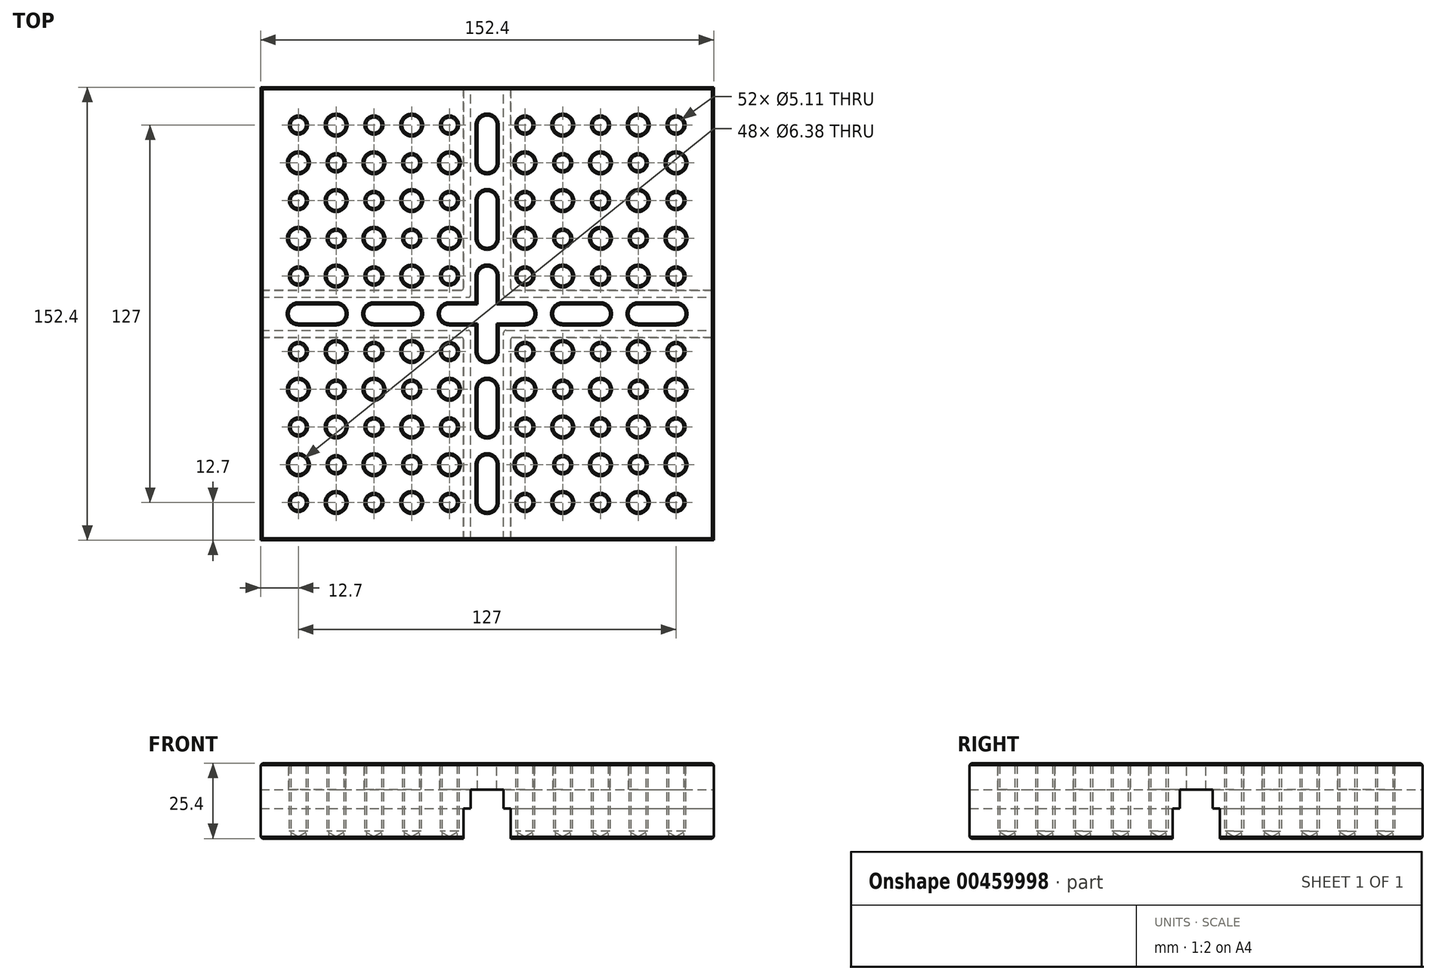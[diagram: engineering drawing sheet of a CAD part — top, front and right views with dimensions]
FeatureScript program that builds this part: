
annotation { "Feature Type Name" : "Feature", "Feature Type Description" : "" }
export const myFeature = defineFeature(function(context is Context, id is Id, definition is map)
    precondition{}
    {
        {
            var Q0;
            Q0=qCreatedBy(makeId("Top.planeOp"),FACE);
            var sketch = newSketch(context, id + "F0", { "sketchPlane" : qUnion([Q0])});
            skLineSegment(sketch, "E0.bottom", {"start": v(-76.2, -76.2) * mm, "end": v(76.2, -76.2) * mm});
            skLineSegment(sketch, "E0.top", {"start": v(-76.2, 76.2) * mm, "end": v(76.2, 76.2) * mm});
            skLineSegment(sketch, "E0.left", {"start": v(-76.2, -76.2) * mm, "end": v(-76.2, 76.2) * mm});
            skLineSegment(sketch, "E0.right", {"start": v(76.2, -76.2) * mm, "end": v(76.2, 76.2) * mm});
            skPoint(sketch, "E0.middle", {"position": v(0, 0) * mm});
            skSolve(sketch);
        }
        {
            var Q0;
            Q0 = qSketchRegion(id + "F0", true);
            extrude(context, id + "F1", {"entities" : qUnion([Q0]), "oppositeDirection" : true, "depth" : 25.4 * mm});
        }
        {
            var Q0;
            Q0=makeQuery(id+"F1.opExtrude","CAP_FACE",FACE,{"disambiguationData":[OSD([sQuery(id+"F0.wireOp",EDGE,"E0.bottom"),sQuery(id+"F0.wireOp",EDGE,"E0.top"),sQuery(id+"F0.wireOp",EDGE,"E0.left"),sQuery(id+"F0.wireOp",EDGE,"E0.right")])],"isStart":true});
            var sketch = newSketch(context, id + "F2", { "sketchPlane" : qUnion([Q0])});
            skPoint(sketch, "E1", {"position": v(-63.5, -63.5) * mm});
            skPoint(sketch, "E2.0.1.0", {"position": v(-63.5, -50.8) * mm});
            skPoint(sketch, "E2.0.2.0", {"position": v(-63.5, -38.1) * mm});
            skPoint(sketch, "E2.0.3.0", {"position": v(-63.5, -25.4) * mm});
            skPoint(sketch, "E2.0.4.0", {"position": v(-63.5, -12.7) * mm});
            skPoint(sketch, "E2.0.5.0", {"position": v(-63.5, 0) * mm});
            skPoint(sketch, "E2.0.6.0", {"position": v(-63.5, 12.7) * mm});
            skPoint(sketch, "E2.0.7.0", {"position": v(-63.5, 25.4) * mm});
            skPoint(sketch, "E2.0.8.0", {"position": v(-63.5, 38.1) * mm});
            skPoint(sketch, "E2.0.9.0", {"position": v(-63.5, 50.8) * mm});
            skPoint(sketch, "E2.0.10.0", {"position": v(-63.5, 63.5) * mm});
            skPoint(sketch, "E2.1.0.0", {"position": v(-50.8, -63.5) * mm});
            skPoint(sketch, "E2.1.1.0", {"position": v(-50.8, -50.8) * mm});
            skPoint(sketch, "E2.1.2.0", {"position": v(-50.8, -38.1) * mm});
            skPoint(sketch, "E2.1.3.0", {"position": v(-50.8, -25.4) * mm});
            skPoint(sketch, "E2.1.4.0", {"position": v(-50.8, -12.7) * mm});
            skPoint(sketch, "E2.1.5.0", {"position": v(-50.8, 0) * mm});
            skPoint(sketch, "E2.1.6.0", {"position": v(-50.8, 12.7) * mm});
            skPoint(sketch, "E2.1.7.0", {"position": v(-50.8, 25.4) * mm});
            skPoint(sketch, "E2.1.8.0", {"position": v(-50.8, 38.1) * mm});
            skPoint(sketch, "E2.1.9.0", {"position": v(-50.8, 50.8) * mm});
            skPoint(sketch, "E2.1.10.0", {"position": v(-50.8, 63.5) * mm});
            skPoint(sketch, "E2.2.0.0", {"position": v(-38.1, -63.5) * mm});
            skPoint(sketch, "E2.2.1.0", {"position": v(-38.1, -50.8) * mm});
            skPoint(sketch, "E2.2.2.0", {"position": v(-38.1, -38.1) * mm});
            skPoint(sketch, "E2.2.3.0", {"position": v(-38.1, -25.4) * mm});
            skPoint(sketch, "E2.2.4.0", {"position": v(-38.1, -12.7) * mm});
            skPoint(sketch, "E2.2.5.0", {"position": v(-38.1, 0) * mm});
            skPoint(sketch, "E2.2.6.0", {"position": v(-38.1, 12.7) * mm});
            skPoint(sketch, "E2.2.7.0", {"position": v(-38.1, 25.4) * mm});
            skPoint(sketch, "E2.2.8.0", {"position": v(-38.1, 38.1) * mm});
            skPoint(sketch, "E2.2.9.0", {"position": v(-38.1, 50.8) * mm});
            skPoint(sketch, "E2.2.10.0", {"position": v(-38.1, 63.5) * mm});
            skPoint(sketch, "E2.3.0.0", {"position": v(-25.4, -63.5) * mm});
            skPoint(sketch, "E2.3.1.0", {"position": v(-25.4, -50.8) * mm});
            skPoint(sketch, "E2.3.2.0", {"position": v(-25.4, -38.1) * mm});
            skPoint(sketch, "E2.3.3.0", {"position": v(-25.4, -25.4) * mm});
            skPoint(sketch, "E2.3.4.0", {"position": v(-25.4, -12.7) * mm});
            skPoint(sketch, "E2.3.5.0", {"position": v(-25.4, 0) * mm});
            skPoint(sketch, "E2.3.6.0", {"position": v(-25.4, 12.7) * mm});
            skPoint(sketch, "E2.3.7.0", {"position": v(-25.4, 25.4) * mm});
            skPoint(sketch, "E2.3.8.0", {"position": v(-25.4, 38.1) * mm});
            skPoint(sketch, "E2.3.9.0", {"position": v(-25.4, 50.8) * mm});
            skPoint(sketch, "E2.3.10.0", {"position": v(-25.4, 63.5) * mm});
            skPoint(sketch, "E2.4.0.0", {"position": v(-12.7, -63.5) * mm});
            skPoint(sketch, "E2.4.1.0", {"position": v(-12.7, -50.8) * mm});
            skPoint(sketch, "E2.4.2.0", {"position": v(-12.7, -38.1) * mm});
            skPoint(sketch, "E2.4.3.0", {"position": v(-12.7, -25.4) * mm});
            skPoint(sketch, "E2.4.4.0", {"position": v(-12.7, -12.7) * mm});
            skPoint(sketch, "E2.4.5.0", {"position": v(-12.7, 0) * mm});
            skPoint(sketch, "E2.4.6.0", {"position": v(-12.7, 12.7) * mm});
            skPoint(sketch, "E2.4.7.0", {"position": v(-12.7, 25.4) * mm});
            skPoint(sketch, "E2.4.8.0", {"position": v(-12.7, 38.1) * mm});
            skPoint(sketch, "E2.4.9.0", {"position": v(-12.7, 50.8) * mm});
            skPoint(sketch, "E2.4.10.0", {"position": v(-12.7, 63.5) * mm});
            skPoint(sketch, "E2.5.0.0", {"position": v(0, -63.5) * mm});
            skPoint(sketch, "E2.5.1.0", {"position": v(0, -50.8) * mm});
            skPoint(sketch, "E2.5.2.0", {"position": v(0, -38.1) * mm});
            skPoint(sketch, "E2.5.3.0", {"position": v(0, -25.4) * mm});
            skPoint(sketch, "E2.5.4.0", {"position": v(0, -12.7) * mm});
            skPoint(sketch, "E2.5.5.0", {"position": v(0, 0) * mm});
            skPoint(sketch, "E2.5.6.0", {"position": v(0, 12.7) * mm});
            skPoint(sketch, "E2.5.7.0", {"position": v(0, 25.4) * mm});
            skPoint(sketch, "E2.5.8.0", {"position": v(0, 38.1) * mm});
            skPoint(sketch, "E2.5.9.0", {"position": v(0, 50.8) * mm});
            skPoint(sketch, "E2.5.10.0", {"position": v(0, 63.5) * mm});
            skPoint(sketch, "E2.6.0.0", {"position": v(12.7, -63.5) * mm});
            skPoint(sketch, "E2.6.1.0", {"position": v(12.7, -50.8) * mm});
            skPoint(sketch, "E2.6.2.0", {"position": v(12.7, -38.1) * mm});
            skPoint(sketch, "E2.6.3.0", {"position": v(12.7, -25.4) * mm});
            skPoint(sketch, "E2.6.4.0", {"position": v(12.7, -12.7) * mm});
            skPoint(sketch, "E2.6.5.0", {"position": v(12.7, 0) * mm});
            skPoint(sketch, "E2.6.6.0", {"position": v(12.7, 12.7) * mm});
            skPoint(sketch, "E2.6.7.0", {"position": v(12.7, 25.4) * mm});
            skPoint(sketch, "E2.6.8.0", {"position": v(12.7, 38.1) * mm});
            skPoint(sketch, "E2.6.9.0", {"position": v(12.7, 50.8) * mm});
            skPoint(sketch, "E2.6.10.0", {"position": v(12.7, 63.5) * mm});
            skPoint(sketch, "E2.7.0.0", {"position": v(25.4, -63.5) * mm});
            skPoint(sketch, "E2.7.1.0", {"position": v(25.4, -50.8) * mm});
            skPoint(sketch, "E2.7.2.0", {"position": v(25.4, -38.1) * mm});
            skPoint(sketch, "E2.7.3.0", {"position": v(25.4, -25.4) * mm});
            skPoint(sketch, "E2.7.4.0", {"position": v(25.4, -12.7) * mm});
            skPoint(sketch, "E2.7.5.0", {"position": v(25.4, 0) * mm});
            skPoint(sketch, "E2.7.6.0", {"position": v(25.4, 12.7) * mm});
            skPoint(sketch, "E2.7.7.0", {"position": v(25.4, 25.4) * mm});
            skPoint(sketch, "E2.7.8.0", {"position": v(25.4, 38.1) * mm});
            skPoint(sketch, "E2.7.9.0", {"position": v(25.4, 50.8) * mm});
            skPoint(sketch, "E2.7.10.0", {"position": v(25.4, 63.5) * mm});
            skPoint(sketch, "E2.8.0.0", {"position": v(38.1, -63.5) * mm});
            skPoint(sketch, "E2.8.1.0", {"position": v(38.1, -50.8) * mm});
            skPoint(sketch, "E2.8.2.0", {"position": v(38.1, -38.1) * mm});
            skPoint(sketch, "E2.8.3.0", {"position": v(38.1, -25.4) * mm});
            skPoint(sketch, "E2.8.4.0", {"position": v(38.1, -12.7) * mm});
            skPoint(sketch, "E2.8.5.0", {"position": v(38.1, 0) * mm});
            skPoint(sketch, "E2.8.6.0", {"position": v(38.1, 12.7) * mm});
            skPoint(sketch, "E2.8.7.0", {"position": v(38.1, 25.4) * mm});
            skPoint(sketch, "E2.8.8.0", {"position": v(38.1, 38.1) * mm});
            skPoint(sketch, "E2.8.9.0", {"position": v(38.1, 50.8) * mm});
            skPoint(sketch, "E2.8.10.0", {"position": v(38.1, 63.5) * mm});
            skPoint(sketch, "E2.9.0.0", {"position": v(50.8, -63.5) * mm});
            skPoint(sketch, "E2.9.1.0", {"position": v(50.8, -50.8) * mm});
            skPoint(sketch, "E2.9.2.0", {"position": v(50.8, -38.1) * mm});
            skPoint(sketch, "E2.9.3.0", {"position": v(50.8, -25.4) * mm});
            skPoint(sketch, "E2.9.4.0", {"position": v(50.8, -12.7) * mm});
            skPoint(sketch, "E2.9.5.0", {"position": v(50.8, 0) * mm});
            skPoint(sketch, "E2.9.6.0", {"position": v(50.8, 12.7) * mm});
            skPoint(sketch, "E2.9.7.0", {"position": v(50.8, 25.4) * mm});
            skPoint(sketch, "E2.9.8.0", {"position": v(50.8, 38.1) * mm});
            skPoint(sketch, "E2.9.9.0", {"position": v(50.8, 50.8) * mm});
            skPoint(sketch, "E2.9.10.0", {"position": v(50.8, 63.5) * mm});
            skPoint(sketch, "E2.10.0.0", {"position": v(63.5, -63.5) * mm});
            skPoint(sketch, "E2.10.1.0", {"position": v(63.5, -50.8) * mm});
            skPoint(sketch, "E2.10.2.0", {"position": v(63.5, -38.1) * mm});
            skPoint(sketch, "E2.10.3.0", {"position": v(63.5, -25.4) * mm});
            skPoint(sketch, "E2.10.4.0", {"position": v(63.5, -12.7) * mm});
            skPoint(sketch, "E2.10.5.0", {"position": v(63.5, 0) * mm});
            skPoint(sketch, "E2.10.6.0", {"position": v(63.5, 12.7) * mm});
            skPoint(sketch, "E2.10.7.0", {"position": v(63.5, 25.4) * mm});
            skPoint(sketch, "E2.10.8.0", {"position": v(63.5, 38.1) * mm});
            skPoint(sketch, "E2.10.9.0", {"position": v(63.5, 50.8) * mm});
            skPoint(sketch, "E2.10.10.0", {"position": v(63.5, 63.5) * mm});
            skLineSegment(sketch, "E2.direction1", {"start": v(-63.5, -63.5) * mm, "end": v(-50.8, -63.5) * mm, "construction": true});
            skLineSegment(sketch, "E2.direction2", {"start": v(-63.5, -63.5) * mm, "end": v(-63.5, -50.8) * mm, "construction": true});
            skSolve(sketch);
        }
        {
            var Q0;
            Q0=sQuery(id+"F2.wireOp",VERTEX,"E2.0.10.0");
            var Q1;
            Q1=sQuery(id+"F2.wireOp",VERTEX,"E2.2.10.0");
            var Q2;
            Q2=sQuery(id+"F2.wireOp",VERTEX,"E2.4.10.0");
            var Q3;
            Q3=sQuery(id+"F2.wireOp",VERTEX,"E2.6.10.0");
            var Q4;
            Q4=sQuery(id+"F2.wireOp",VERTEX,"E2.8.10.0");
            var Q5;
            Q5=sQuery(id+"F2.wireOp",VERTEX,"E2.10.10.0");
            var Q6;
            Q6=sQuery(id+"F2.wireOp",VERTEX,"E2.1.9.0");
            var Q7;
            Q7=sQuery(id+"F2.wireOp",VERTEX,"E2.3.9.0");
            var Q8;
            Q8=sQuery(id+"F2.wireOp",VERTEX,"E2.7.9.0");
            var Q9;
            Q9=sQuery(id+"F2.wireOp",VERTEX,"E2.9.9.0");
            var Q10;
            Q10=sQuery(id+"F2.wireOp",VERTEX,"E2.0.8.0");
            var Q11;
            Q11=sQuery(id+"F2.wireOp",VERTEX,"E2.2.8.0");
            var Q12;
            Q12=sQuery(id+"F2.wireOp",VERTEX,"E2.4.8.0");
            var Q13;
            Q13=sQuery(id+"F2.wireOp",VERTEX,"E2.6.8.0");
            var Q14;
            Q14=sQuery(id+"F2.wireOp",VERTEX,"E2.10.8.0");
            var Q15;
            Q15=sQuery(id+"F2.wireOp",VERTEX,"E2.8.8.0");
            var Q16;
            Q16=sQuery(id+"F2.wireOp",VERTEX,"E2.1.7.0");
            var Q17;
            Q17=sQuery(id+"F2.wireOp",VERTEX,"E2.3.7.0");
            var Q18;
            Q18=sQuery(id+"F2.wireOp",VERTEX,"E2.3.7.0");
            var Q19;
            Q19=sQuery(id+"F2.wireOp",VERTEX,"E2.7.7.0");
            var Q20;
            Q20=sQuery(id+"F2.wireOp",VERTEX,"E2.9.7.0");
            var Q21;
            Q21=sQuery(id+"F2.wireOp",VERTEX,"E2.0.6.0");
            var Q22;
            Q22=sQuery(id+"F2.wireOp",VERTEX,"E2.2.6.0");
            var Q23;
            Q23=sQuery(id+"F2.wireOp",VERTEX,"E2.4.6.0");
            var Q24;
            Q24=sQuery(id+"F2.wireOp",VERTEX,"E2.6.6.0");
            var Q25;
            Q25=sQuery(id+"F2.wireOp",VERTEX,"E2.8.6.0");
            var Q26;
            Q26=sQuery(id+"F2.wireOp",VERTEX,"E2.10.6.0");
            var Q27;
            Q27=makeQuery(id+"F1.opExtrude","SWEPT_BODY",BODY,{"disambiguationData":[OSD([sQuery(id+"F0.wireOp",EDGE,"E0.bottom"),sQuery(id+"F0.wireOp",EDGE,"E0.top"),sQuery(id+"F0.wireOp",EDGE,"E0.left"),sQuery(id+"F0.wireOp",EDGE,"E0.right")])]});
            hole(context, id + "F3", {"style" : HoleStyle.SIMPLE, "endStyle" : HoleEndStyle.THROUGH, "standardTappedOrClearance" : lookupTablePath({ "standard" : "ANSI", "engagement" : "75%", "pitch" : "20 tpi", "size" : "1/4", "type" : "Tapped" }), "standardBlindInLast" : lookupTablePath({ "standard" : "ANSI", "engagement" : "75%", "pitch" : "20 tpi", "size" : "1/4", "type" : "Tapped" }), "holeDiameter" : 5.1 * mm, "showTappedDepth" : true, "isTappedThrough" : true, "tappedDepth" : 19.05 * mm, "tapClearance" : 3, "locations" : qUnion([Q0, Q1, Q2, Q3, Q4, Q5, Q6, Q7, Q8, Q9, Q10, Q11, Q12, Q13, Q14, Q15, Q16, Q17, Q18, Q19, Q20, Q21, Q22, Q23, Q24, Q25, Q26]), "scope" : qUnion([Q27]), "majorDiameter" : 6.35 * mm, "startStyle" : HoleStartStyle.PART});
        }
        {
            var Q0;
            Q0=sQuery(id+"F2.wireOp",VERTEX,"E2.0.4.0");
            var Q1;
            Q1=sQuery(id+"F2.wireOp",VERTEX,"E2.2.4.0");
            var Q2;
            Q2=sQuery(id+"F2.wireOp",VERTEX,"E2.4.4.0");
            var Q3;
            Q3=sQuery(id+"F2.wireOp",VERTEX,"E2.6.4.0");
            var Q4;
            Q4=sQuery(id+"F2.wireOp",VERTEX,"E2.8.4.0");
            var Q5;
            Q5=sQuery(id+"F2.wireOp",VERTEX,"E2.10.4.0");
            var Q6;
            Q6=sQuery(id+"F2.wireOp",VERTEX,"E2.1.3.0");
            var Q7;
            Q7=sQuery(id+"F2.wireOp",VERTEX,"E2.3.3.0");
            var Q8;
            Q8=sQuery(id+"F2.wireOp",VERTEX,"E2.7.3.0");
            var Q9;
            Q9=sQuery(id+"F2.wireOp",VERTEX,"E2.9.3.0");
            var Q10;
            Q10=sQuery(id+"F2.wireOp",VERTEX,"E2.10.2.0");
            var Q11;
            Q11=sQuery(id+"F2.wireOp",VERTEX,"E2.8.2.0");
            var Q12;
            Q12=sQuery(id+"F2.wireOp",VERTEX,"E2.6.2.0");
            var Q13;
            Q13=sQuery(id+"F2.wireOp",VERTEX,"E2.4.2.0");
            var Q14;
            Q14=sQuery(id+"F2.wireOp",VERTEX,"E2.2.2.0");
            var Q15;
            Q15=sQuery(id+"F2.wireOp",VERTEX,"E2.0.2.0");
            var Q16;
            Q16=sQuery(id+"F2.wireOp",VERTEX,"E2.1.1.0");
            var Q17;
            Q17=sQuery(id+"F2.wireOp",VERTEX,"E2.3.1.0");
            var Q18;
            Q18=sQuery(id+"F2.wireOp",VERTEX,"E2.9.1.0");
            var Q19;
            Q19=sQuery(id+"F2.wireOp",VERTEX,"E2.7.1.0");
            var Q20;
            Q20=sQuery(id+"F2.wireOp",VERTEX,"E1");
            var Q21;
            Q21=sQuery(id+"F2.wireOp",VERTEX,"E2.2.0.0");
            var Q22;
            Q22=sQuery(id+"F2.wireOp",VERTEX,"E2.4.0.0");
            var Q23;
            Q23=sQuery(id+"F2.wireOp",VERTEX,"E2.6.0.0");
            var Q24;
            Q24=sQuery(id+"F2.wireOp",VERTEX,"E2.8.0.0");
            var Q25;
            Q25=sQuery(id+"F2.wireOp",VERTEX,"E2.10.0.0");
            var Q26;
            Q26=makeQuery(id+"F1.opExtrude","SWEPT_BODY",BODY,{"disambiguationData":[OSD([sQuery(id+"F0.wireOp",EDGE,"E0.bottom"),sQuery(id+"F0.wireOp",EDGE,"E0.top"),sQuery(id+"F0.wireOp",EDGE,"E0.left"),sQuery(id+"F0.wireOp",EDGE,"E0.right")])]});
            hole(context, id + "F4", {"style" : HoleStyle.SIMPLE, "endStyle" : HoleEndStyle.THROUGH, "standardTappedOrClearance" : lookupTablePath({ "standard" : "ANSI", "engagement" : "75%", "pitch" : "20 tpi", "size" : "1/4", "type" : "Tapped" }), "standardBlindInLast" : lookupTablePath({ "standard" : "ANSI", "engagement" : "75%", "pitch" : "20 tpi", "size" : "1/4", "type" : "Tapped" }), "holeDiameter" : 5.1 * mm, "showTappedDepth" : true, "isTappedThrough" : true, "tappedDepth" : 19.05 * mm, "tapClearance" : 3, "locations" : qUnion([Q0, Q1, Q2, Q3, Q4, Q5, Q6, Q7, Q8, Q9, Q10, Q11, Q12, Q13, Q14, Q15, Q16, Q17, Q18, Q19, Q20, Q21, Q22, Q23, Q24, Q25]), "scope" : qUnion([Q26]), "majorDiameter" : 6.35 * mm, "startStyle" : HoleStartStyle.PART});
        }
        {
            var Q0;
            Q0=sQuery(id+"F2.wireOp",VERTEX,"E2.1.10.0");
            var Q1;
            Q1=sQuery(id+"F2.wireOp",VERTEX,"E2.3.10.0");
            var Q2;
            Q2=sQuery(id+"F2.wireOp",VERTEX,"E2.7.10.0");
            var Q3;
            Q3=sQuery(id+"F2.wireOp",VERTEX,"E2.9.10.0");
            var Q4;
            Q4=sQuery(id+"F2.wireOp",VERTEX,"E2.9.8.0");
            var Q5;
            Q5=sQuery(id+"F2.wireOp",VERTEX,"E2.8.9.0");
            var Q6;
            Q6=sQuery(id+"F2.wireOp",VERTEX,"E2.6.9.0");
            var Q7;
            Q7=sQuery(id+"F2.wireOp",VERTEX,"E2.4.9.0");
            var Q8;
            Q8=sQuery(id+"F2.wireOp",VERTEX,"E2.0.9.0");
            var Q9;
            Q9=sQuery(id+"F2.wireOp",VERTEX,"E2.1.8.0");
            var Q10;
            Q10=sQuery(id+"F2.wireOp",VERTEX,"E2.2.9.0");
            var Q11;
            Q11=sQuery(id+"F2.wireOp",VERTEX,"E2.3.8.0");
            var Q12;
            Q12=sQuery(id+"F2.wireOp",VERTEX,"E2.7.8.0");
            var Q13;
            Q13=sQuery(id+"F2.wireOp",VERTEX,"E2.10.9.0");
            var Q14;
            Q14=sQuery(id+"F2.wireOp",VERTEX,"E2.10.7.0");
            var Q15;
            Q15=sQuery(id+"F2.wireOp",VERTEX,"E2.8.7.0");
            var Q16;
            Q16=sQuery(id+"F2.wireOp",VERTEX,"E2.10.7.0");
            var Q17;
            Q17=sQuery(id+"F2.wireOp",VERTEX,"E2.6.7.0");
            var Q18;
            Q18=sQuery(id+"F2.wireOp",VERTEX,"E2.4.7.0");
            var Q19;
            Q19=sQuery(id+"F2.wireOp",VERTEX,"E2.0.7.0");
            var Q20;
            Q20=sQuery(id+"F2.wireOp",VERTEX,"E2.3.6.0");
            var Q21;
            Q21=sQuery(id+"F2.wireOp",VERTEX,"E2.1.6.0");
            var Q22;
            Q22=sQuery(id+"F2.wireOp",VERTEX,"E2.2.7.0");
            var Q23;
            Q23=sQuery(id+"F2.wireOp",VERTEX,"E2.7.6.0");
            var Q24;
            Q24=sQuery(id+"F2.wireOp",VERTEX,"E2.9.6.0");
            var Q25;
            Q25=sQuery(id+"F2.wireOp",VERTEX,"E2.1.4.0");
            var Q26;
            Q26=sQuery(id+"F2.wireOp",VERTEX,"E2.3.4.0");
            var Q27;
            Q27=sQuery(id+"F2.wireOp",VERTEX,"E2.4.3.0");
            var Q28;
            Q28=sQuery(id+"F2.wireOp",VERTEX,"E2.2.3.0");
            var Q29;
            Q29=sQuery(id+"F2.wireOp",VERTEX,"E2.0.3.0");
            var Q30;
            Q30=sQuery(id+"F2.wireOp",VERTEX,"E2.1.2.0");
            var Q31;
            Q31=sQuery(id+"F2.wireOp",VERTEX,"E2.3.2.0");
            var Q32;
            Q32=sQuery(id+"F2.wireOp",VERTEX,"E2.0.1.0");
            var Q33;
            Q33=sQuery(id+"F2.wireOp",VERTEX,"E2.2.1.0");
            var Q34;
            Q34=sQuery(id+"F2.wireOp",VERTEX,"E2.4.1.0");
            var Q35;
            Q35=sQuery(id+"F2.wireOp",VERTEX,"E2.3.0.0");
            var Q36;
            Q36=sQuery(id+"F2.wireOp",VERTEX,"E2.1.0.0");
            var Q37;
            Q37=sQuery(id+"F2.wireOp",VERTEX,"E2.3.0.0");
            var Q38;
            Q38=sQuery(id+"F2.wireOp",VERTEX,"E2.7.0.0");
            var Q39;
            Q39=sQuery(id+"F2.wireOp",VERTEX,"E2.6.1.0");
            var Q40;
            Q40=sQuery(id+"F2.wireOp",VERTEX,"E2.6.3.0");
            var Q41;
            Q41=sQuery(id+"F2.wireOp",VERTEX,"E2.7.4.0");
            var Q42;
            Q42=sQuery(id+"F2.wireOp",VERTEX,"E2.7.2.0");
            var Q43;
            Q43=sQuery(id+"F2.wireOp",VERTEX,"E2.8.3.0");
            var Q44;
            Q44=sQuery(id+"F2.wireOp",VERTEX,"E2.9.4.0");
            var Q45;
            Q45=sQuery(id+"F2.wireOp",VERTEX,"E2.10.3.0");
            var Q46;
            Q46=sQuery(id+"F2.wireOp",VERTEX,"E2.8.1.0");
            var Q47;
            Q47=sQuery(id+"F2.wireOp",VERTEX,"E2.9.2.0");
            var Q48;
            Q48=sQuery(id+"F2.wireOp",VERTEX,"E2.10.1.0");
            var Q49;
            Q49=sQuery(id+"F2.wireOp",VERTEX,"E2.9.0.0");
            var Q50;
            Q50=makeQuery(id+"F1.opExtrude","SWEPT_BODY",BODY,{"disambiguationData":[OSD([sQuery(id+"F0.wireOp",EDGE,"E0.bottom"),sQuery(id+"F0.wireOp",EDGE,"E0.top"),sQuery(id+"F0.wireOp",EDGE,"E0.left"),sQuery(id+"F0.wireOp",EDGE,"E0.right")])]});
            hole(context, id + "F5", {"style" : HoleStyle.SIMPLE, "endStyle" : HoleEndStyle.BLIND, "holeDiameter" : 6.38 * mm, "holeDepth" : 22.86 * mm, "isTappedThrough" : true, "tappedDepth" : 19.05 * mm, "tapClearance" : 3, "locations" : qUnion([Q0, Q1, Q2, Q3, Q4, Q5, Q6, Q7, Q8, Q9, Q10, Q11, Q12, Q13, Q14, Q15, Q16, Q17, Q18, Q19, Q20, Q21, Q22, Q23, Q24, Q25, Q26, Q27, Q28, Q29, Q30, Q31, Q32, Q33, Q34, Q35, Q36, Q37, Q38, Q39, Q40, Q41, Q42, Q43, Q44, Q45, Q46, Q47, Q48, Q49]), "scope" : qUnion([Q50]), "startStyle" : HoleStartStyle.PART});
        }
        {
            var Q0;
            Q0=makeQuery(id+"F2.imprint","IMPRINT",FACE,{"disambiguationData":[TD([[makeQuery(id+"F2.imprint","IMPRINT",EDGE,{"derivedFrom":makeQuery(id+"F1.opExtrude","CAP_EDGE",EDGE,{"disambiguationData":[OSD([sQuery(id+"F0.wireOp",EDGE,"E0.bottom")])],"isStart":true})}),1.0]])]});
            var sketch = newSketch(context, id + "F6", { "sketchPlane" : qUnion([Q0])});
            skLineSegment(sketch, "E3", {"start": v(0, 63.5) * mm, "end": v(0, 50.8) * mm});
            skLineSegment(sketch, "E4", {"start": v(0, 38.1) * mm, "end": v(0, 25.4) * mm});
            skLineSegment(sketch, "E5", {"start": v(0, 12.7) * mm, "end": v(0, -12.7) * mm});
            skLineSegment(sketch, "E6", {"start": v(12.7, 0) * mm, "end": v(-12.7, 0) * mm});
            skLineSegment(sketch, "E7", {"start": v(-25.4, 0) * mm, "end": v(-38.1, 0) * mm});
            skLineSegment(sketch, "E8", {"start": v(-50.8, 0) * mm, "end": v(-63.5, 0) * mm});
            skLineSegment(sketch, "E9", {"start": v(25.4, 0) * mm, "end": v(38.1, 0) * mm});
            skLineSegment(sketch, "E10", {"start": v(50.8, 0) * mm, "end": v(63.5, 0) * mm});
            skLineSegment(sketch, "E11.MirrorCS", {"start": v(0, -38.1) * mm, "end": v(0, -25.4) * mm});
            skLineSegment(sketch, "E12.MirrorCS", {"start": v(0, -63.5) * mm, "end": v(0, -50.8) * mm});
            skArc(sketch, "E13.0.startCap", {"start": v(-3.24, 63.5) * mm, "mid": v(0, 66.74) * mm, "end": v(3.24, 63.5) * mm});
            skArc(sketch, "E13.0.endCap", {"start": v(3.24, 50.8) * mm, "mid": v(0, 47.56) * mm, "end": v(-3.24, 50.8) * mm});
            skLineSegment(sketch, "E13.0.left", {"start": v(3.24, 63.5) * mm, "end": v(3.24, 50.8) * mm});
            skLineSegment(sketch, "E13.0.right", {"start": v(-3.24, 63.5) * mm, "end": v(-3.24, 50.8) * mm});
            skArc(sketch, "E14.0.startCap", {"start": v(-3.24, 38.1) * mm, "mid": v(0, 41.34) * mm, "end": v(3.24, 38.1) * mm});
            skArc(sketch, "E14.0.endCap", {"start": v(3.24, 25.4) * mm, "mid": v(0, 22.16) * mm, "end": v(-3.24, 25.4) * mm});
            skLineSegment(sketch, "E14.0.left", {"start": v(3.24, 38.1) * mm, "end": v(3.24, 25.4) * mm});
            skLineSegment(sketch, "E14.0.right", {"start": v(-3.24, 38.1) * mm, "end": v(-3.24, 25.4) * mm});
            skArc(sketch, "E14.1.startCap", {"start": v(-3.24, 12.7) * mm, "mid": v(0, 15.94) * mm, "end": v(3.24, 12.7) * mm});
            skArc(sketch, "E14.1.endCap", {"start": v(3.24, -12.7) * mm, "mid": v(0, -15.94) * mm, "end": v(-3.24, -12.7) * mm});
            skLineSegment(sketch, "E14.1.left", {"start": v(3.24, 12.7) * mm, "end": v(3.24, -12.7) * mm});
            skLineSegment(sketch, "E14.1.right", {"start": v(-3.24, 12.7) * mm, "end": v(-3.24, -12.7) * mm});
            skArc(sketch, "E14.2.startCap", {"start": v(12.7, 3.24) * mm, "mid": v(15.94, 0) * mm, "end": v(12.7, -3.24) * mm});
            skArc(sketch, "E14.2.endCap", {"start": v(-12.7, -3.24) * mm, "mid": v(-15.94, 0) * mm, "end": v(-12.7, 3.24) * mm});
            skLineSegment(sketch, "E14.2.left", {"start": v(12.7, -3.24) * mm, "end": v(-12.7, -3.24) * mm});
            skLineSegment(sketch, "E14.2.right", {"start": v(12.7, 3.24) * mm, "end": v(-12.7, 3.24) * mm});
            skArc(sketch, "E14.3.startCap", {"start": v(-25.4, 3.24) * mm, "mid": v(-22.16, 0) * mm, "end": v(-25.4, -3.24) * mm});
            skArc(sketch, "E14.3.endCap", {"start": v(-38.1, -3.24) * mm, "mid": v(-41.34, 0) * mm, "end": v(-38.1, 3.24) * mm});
            skLineSegment(sketch, "E14.3.left", {"start": v(-25.4, -3.24) * mm, "end": v(-38.1, -3.24) * mm});
            skLineSegment(sketch, "E14.3.right", {"start": v(-25.4, 3.24) * mm, "end": v(-38.1, 3.24) * mm});
            skArc(sketch, "E14.4.startCap", {"start": v(-50.8, 3.24) * mm, "mid": v(-47.56, 0) * mm, "end": v(-50.8, -3.24) * mm});
            skArc(sketch, "E14.4.endCap", {"start": v(-63.5, -3.24) * mm, "mid": v(-66.74, 0) * mm, "end": v(-63.5, 3.24) * mm});
            skLineSegment(sketch, "E14.4.left", {"start": v(-50.8, -3.24) * mm, "end": v(-63.5, -3.24) * mm});
            skLineSegment(sketch, "E14.4.right", {"start": v(-50.8, 3.24) * mm, "end": v(-63.5, 3.24) * mm});
            skArc(sketch, "E14.5.startCap", {"start": v(25.4, -3.24) * mm, "mid": v(22.16, 0) * mm, "end": v(25.4, 3.24) * mm});
            skArc(sketch, "E14.5.endCap", {"start": v(38.1, 3.24) * mm, "mid": v(41.34, 0) * mm, "end": v(38.1, -3.24) * mm});
            skLineSegment(sketch, "E14.5.left", {"start": v(25.4, 3.24) * mm, "end": v(38.1, 3.24) * mm});
            skLineSegment(sketch, "E14.5.right", {"start": v(25.4, -3.24) * mm, "end": v(38.1, -3.24) * mm});
            skArc(sketch, "E14.6.startCap", {"start": v(50.8, -3.24) * mm, "mid": v(47.56, 0) * mm, "end": v(50.8, 3.24) * mm});
            skArc(sketch, "E14.6.endCap", {"start": v(63.5, 3.24) * mm, "mid": v(66.74, 0) * mm, "end": v(63.5, -3.24) * mm});
            skLineSegment(sketch, "E14.6.left", {"start": v(50.8, 3.24) * mm, "end": v(63.5, 3.24) * mm});
            skLineSegment(sketch, "E14.6.right", {"start": v(50.8, -3.24) * mm, "end": v(63.5, -3.24) * mm});
            skArc(sketch, "E14.7.startCap", {"start": v(3.24, -38.1) * mm, "mid": v(0, -41.34) * mm, "end": v(-3.24, -38.1) * mm});
            skArc(sketch, "E14.7.endCap", {"start": v(-3.24, -25.4) * mm, "mid": v(0, -22.16) * mm, "end": v(3.24, -25.4) * mm});
            skLineSegment(sketch, "E14.7.left", {"start": v(-3.24, -38.1) * mm, "end": v(-3.24, -25.4) * mm});
            skLineSegment(sketch, "E14.7.right", {"start": v(3.24, -38.1) * mm, "end": v(3.24, -25.4) * mm});
            skArc(sketch, "E14.8.startCap", {"start": v(3.24, -63.5) * mm, "mid": v(0, -66.74) * mm, "end": v(-3.24, -63.5) * mm});
            skArc(sketch, "E14.8.endCap", {"start": v(-3.24, -50.8) * mm, "mid": v(0, -47.56) * mm, "end": v(3.24, -50.8) * mm});
            skLineSegment(sketch, "E14.8.left", {"start": v(-3.24, -63.5) * mm, "end": v(-3.24, -50.8) * mm});
            skLineSegment(sketch, "E14.8.right", {"start": v(3.24, -63.5) * mm, "end": v(3.24, -50.8) * mm});
            skSolve(sketch);
        }
        {
            var Q0;
            Q0 = qSketchRegion(id + "F6", true);
            var Q1;
            Q1 = qConstructionFilter(qBodyType(qCreatedBy(id + "F6" ,EDGE), BodyType.WIRE), ConstructionObject.NO);
            extrude(context, id + "F7", {"entities" : qUnion([Q0]), "operationType" : NewBodyOperationType.REMOVE, "surfaceEntities" : qUnion([Q1]), "endBound" : BoundingType.THROUGH_ALL, "oppositeDirection" : true, "depth" : 25.4 * mm});
        }
        {
            var Q0;
            Q0=makeQuery(id+"F1.opExtrude","CAP_FACE",FACE,{"disambiguationData":[OSD([sQuery(id+"F0.wireOp",EDGE,"E0.bottom"),sQuery(id+"F0.wireOp",EDGE,"E0.top"),sQuery(id+"F0.wireOp",EDGE,"E0.left"),sQuery(id+"F0.wireOp",EDGE,"E0.right")])],"isStart":true});
            var Q1;
            Q1=makeQuery(id+"F1.opExtrude","CAP_FACE",FACE,{"disambiguationData":[OSD([sQuery(id+"F0.wireOp",EDGE,"E0.bottom"),sQuery(id+"F0.wireOp",EDGE,"E0.top"),sQuery(id+"F0.wireOp",EDGE,"E0.left"),sQuery(id+"F0.wireOp",EDGE,"E0.right")])],"isStart":false});
            chamfer(context, id + "F8", {"entities" : qUnion([Q0, Q1]), "width" : 0.64 * mm, "tangentPropagation" : true});
        }
        {
            var Q0;
            Q0=makeQuery(id+"F1.opExtrude","SWEPT_FACE",FACE,{"disambiguationData":[OSD([sQuery(id+"F0.wireOp",EDGE,"E0.right")])]});
            var sketch = newSketch(context, id + "F9", { "sketchPlane" : qUnion([Q0])});
            skLineSegment(sketch, "E15.bottom", {"start": v(-7.94, -34.3) * mm, "end": v(7.94, -34.3) * mm});
            skLineSegment(sketch, "E15.top", {"start": v(-7.94, -15.24) * mm, "end": v(-5.56, -15.24) * mm});
            skLineSegment(sketch, "E15.left", {"start": v(-7.94, -34.3) * mm, "end": v(-7.94, -15.24) * mm});
            skLineSegment(sketch, "E15.right", {"start": v(7.94, -34.3) * mm, "end": v(7.94, -15.24) * mm});
            skPoint(sketch, "E15.middle", {"position": v(0, -24.77) * mm});
            skLineSegment(sketch, "E16.top", {"start": v(-5.56, -8.89) * mm, "end": v(5.56, -8.89) * mm});
            skLineSegment(sketch, "E16.left", {"start": v(-5.56, -15.24) * mm, "end": v(-5.56, -8.89) * mm});
            skLineSegment(sketch, "E16.right", {"start": v(5.56, -15.24) * mm, "end": v(5.56, -8.89) * mm});
            skPoint(sketch, "E16.middle", {"position": v(0, -15.24) * mm});
            skLineSegment(sketch, "E17.trimOffspring", {"start": v(5.56, -15.24) * mm, "end": v(7.94, -15.24) * mm});
            skPoint(sketch, "E16.bottom.end.orphan", {"position": v(5.56, -21.59) * mm});
            skPoint(sketch, "E16.bottom.start.orphan", {"position": v(-5.56, -21.59) * mm});
            skSolve(sketch);
        }
        {
            var Q0;
            Q0 = qSketchRegion(id + "F9", true);
            extrude(context, id + "F10", {"entities" : qUnion([Q0]), "operationType" : NewBodyOperationType.REMOVE, "endBound" : BoundingType.THROUGH_ALL, "oppositeDirection" : true, "depth" : 25.4 * mm});
        }
        {
            var Q0;
            Q0=makeQuery(id+"F1.opExtrude","SWEPT_FACE",FACE,{"disambiguationData":[OSD([sQuery(id+"F0.wireOp",EDGE,"E0.top")])]});
            var sketch = newSketch(context, id + "F11", { "sketchPlane" : qUnion([Q0])});
            skLineSegment(sketch, "E18.bottom", {"start": v(-7.94, -34.3) * mm, "end": v(7.94, -34.3) * mm});
            skLineSegment(sketch, "E18.top", {"start": v(-7.94, -15.24) * mm, "end": v(-5.56, -15.24) * mm});
            skLineSegment(sketch, "E18.left", {"start": v(-7.94, -34.3) * mm, "end": v(-7.94, -15.24) * mm});
            skLineSegment(sketch, "E18.right", {"start": v(7.94, -34.3) * mm, "end": v(7.94, -15.24) * mm});
            skPoint(sketch, "E18.middle", {"position": v(0, -24.77) * mm});
            skLineSegment(sketch, "E19.top", {"start": v(-5.56, -8.9) * mm, "end": v(5.56, -8.9) * mm});
            skLineSegment(sketch, "E19.left", {"start": v(-5.56, -15.24) * mm, "end": v(-5.56, -8.9) * mm});
            skLineSegment(sketch, "E19.right", {"start": v(5.56, -15.24) * mm, "end": v(5.56, -8.9) * mm});
            skPoint(sketch, "E19.middle", {"position": v(0, -15.24) * mm});
            skLineSegment(sketch, "E20.trimOffspring", {"start": v(5.56, -15.24) * mm, "end": v(7.94, -15.24) * mm});
            skPoint(sketch, "E21.orphan", {"position": v(-5.56, -21.59) * mm});
            skPoint(sketch, "E22.orphan", {"position": v(5.56, -21.59) * mm});
            skSolve(sketch);
        }
        {
            var Q0;
            Q0 = qSketchRegion(id + "F11", true);
            extrude(context, id + "F12", {"entities" : qUnion([Q0]), "operationType" : NewBodyOperationType.REMOVE, "endBound" : BoundingType.THROUGH_ALL, "oppositeDirection" : true, "depth" : 25.4 * mm});
        }
        {
            var Q0;
            {var subQ0=sQuery(id+"F0.wireOp",EDGE,"E0.right");Q0=makeQuery(id+"F12.boolean.opBoolean","INTERSECT",EDGE,{"derivedFrom":[makeQuery(id+"F10.boolean.opBoolean","COPY",FACE,{"disambiguationData":[TD([makeQuery(id+"F1.opExtrude","SWEPT_FACE",FACE,{"disambiguationData":[OSD([subQ0])]})])],"derivedFrom":makeQuery(id+"F10.opExtrude","SWEPT_FACE",FACE,{"disambiguationData":[OSD([sQuery(id+"F9.wireOp",EDGE,"E15.left")])]})}),makeQuery(id+"F12.opExtrude","SWEPT_FACE",FACE,{"disambiguationData":[OSD([sQuery(id+"F11.wireOp",EDGE,"E18.left")])]})]});}
            var Q1;
            {var subQ3=sQuery(id+"F0.wireOp",EDGE,"E0.left");Q1=makeQuery(id+"F12.boolean.opBoolean","INTERSECT",EDGE,{"derivedFrom":[makeQuery(id+"F10.boolean.opBoolean","COPY",FACE,{"disambiguationData":[TD([makeQuery(id+"F1.opExtrude","SWEPT_FACE",FACE,{"disambiguationData":[OSD([subQ3])]})])],"derivedFrom":makeQuery(id+"F10.opExtrude","SWEPT_FACE",FACE,{"disambiguationData":[OSD([sQuery(id+"F9.wireOp",EDGE,"E15.left")])]})}),makeQuery(id+"F12.opExtrude","SWEPT_FACE",FACE,{"disambiguationData":[OSD([sQuery(id+"F11.wireOp",EDGE,"E18.right")])]})]});}
            var Q2;
            {var subQ0=sQuery(id+"F0.wireOp",EDGE,"E0.right");Q2=makeQuery(id+"F12.boolean.opBoolean","INTERSECT",EDGE,{"derivedFrom":[makeQuery(id+"F10.boolean.opBoolean","COPY",FACE,{"disambiguationData":[TD([makeQuery(id+"F1.opExtrude","SWEPT_FACE",FACE,{"disambiguationData":[OSD([subQ0])]})])],"derivedFrom":makeQuery(id+"F10.opExtrude","SWEPT_FACE",FACE,{"disambiguationData":[OSD([sQuery(id+"F9.wireOp",EDGE,"E15.right")])]})}),makeQuery(id+"F12.opExtrude","SWEPT_FACE",FACE,{"disambiguationData":[OSD([sQuery(id+"F11.wireOp",EDGE,"E18.left")])]})]});}
            var Q3;
            {var subQ2=sQuery(id+"F0.wireOp",EDGE,"E0.left");Q3=makeQuery(id+"F12.boolean.opBoolean","INTERSECT",EDGE,{"derivedFrom":[makeQuery(id+"F10.boolean.opBoolean","COPY",FACE,{"disambiguationData":[TD([makeQuery(id+"F1.opExtrude","SWEPT_FACE",FACE,{"disambiguationData":[OSD([subQ2])]})])],"derivedFrom":makeQuery(id+"F10.opExtrude","SWEPT_FACE",FACE,{"disambiguationData":[OSD([sQuery(id+"F9.wireOp",EDGE,"E15.right")])]})}),makeQuery(id+"F12.opExtrude","SWEPT_FACE",FACE,{"disambiguationData":[OSD([sQuery(id+"F11.wireOp",EDGE,"E18.right")])]})]});}
            var Q4;
            Q4=makeQuery(id+"F12.boolean.opBoolean","INTERSECT",EDGE,{"derivedFrom":[makeQuery(id+"F10.boolean.opBoolean","COPY",FACE,{"disambiguationData":[TD([makeQuery(id+"F1.opExtrude","SWEPT_FACE",FACE,{"disambiguationData":[OSD([sQuery(id+"F0.wireOp",EDGE,"E0.left")])]})])],"derivedFrom":makeQuery(id+"F10.opExtrude","SWEPT_FACE",FACE,{"disambiguationData":[OSD([sQuery(id+"F9.wireOp",EDGE,"E16.right")])]})}),makeQuery(id+"F12.opExtrude","SWEPT_FACE",FACE,{"disambiguationData":[OSD([sQuery(id+"F11.wireOp",EDGE,"E19.right")])]})]});
            var Q5;
            Q5=makeQuery(id+"F12.boolean.opBoolean","INTERSECT",EDGE,{"derivedFrom":[makeQuery(id+"F10.boolean.opBoolean","COPY",FACE,{"disambiguationData":[TD([makeQuery(id+"F1.opExtrude","SWEPT_FACE",FACE,{"disambiguationData":[OSD([sQuery(id+"F0.wireOp",EDGE,"E0.left")])]})])],"derivedFrom":makeQuery(id+"F10.opExtrude","SWEPT_FACE",FACE,{"disambiguationData":[OSD([sQuery(id+"F9.wireOp",EDGE,"E16.left")])]})}),makeQuery(id+"F12.opExtrude","SWEPT_FACE",FACE,{"disambiguationData":[OSD([sQuery(id+"F11.wireOp",EDGE,"E19.right")])]})]});
            var Q6;
            Q6=makeQuery(id+"F12.boolean.opBoolean","INTERSECT",EDGE,{"derivedFrom":[makeQuery(id+"F10.boolean.opBoolean","COPY",FACE,{"disambiguationData":[TD([makeQuery(id+"F1.opExtrude","SWEPT_FACE",FACE,{"disambiguationData":[OSD([sQuery(id+"F0.wireOp",EDGE,"E0.right")])]})])],"derivedFrom":makeQuery(id+"F10.opExtrude","SWEPT_FACE",FACE,{"disambiguationData":[OSD([sQuery(id+"F9.wireOp",EDGE,"E16.left")])]})}),makeQuery(id+"F12.opExtrude","SWEPT_FACE",FACE,{"disambiguationData":[OSD([sQuery(id+"F11.wireOp",EDGE,"E19.left")])]})]});
            var Q7;
            Q7=makeQuery(id+"F12.boolean.opBoolean","INTERSECT",EDGE,{"derivedFrom":[makeQuery(id+"F10.boolean.opBoolean","COPY",FACE,{"disambiguationData":[TD([makeQuery(id+"F1.opExtrude","SWEPT_FACE",FACE,{"disambiguationData":[OSD([sQuery(id+"F0.wireOp",EDGE,"E0.right")])]})])],"derivedFrom":makeQuery(id+"F10.opExtrude","SWEPT_FACE",FACE,{"disambiguationData":[OSD([sQuery(id+"F9.wireOp",EDGE,"E16.right")])]})}),makeQuery(id+"F12.opExtrude","SWEPT_FACE",FACE,{"disambiguationData":[OSD([sQuery(id+"F11.wireOp",EDGE,"E19.left")])]})]});
            fillet(context, id + "F13", {"entities" : qUnion([Q0, Q1, Q2, Q3, Q4, Q5, Q6, Q7]), "radius" : 0.8 * mm, "tangentPropagation" : true, "allowEdgeOverflow" : false});
        }
    });
